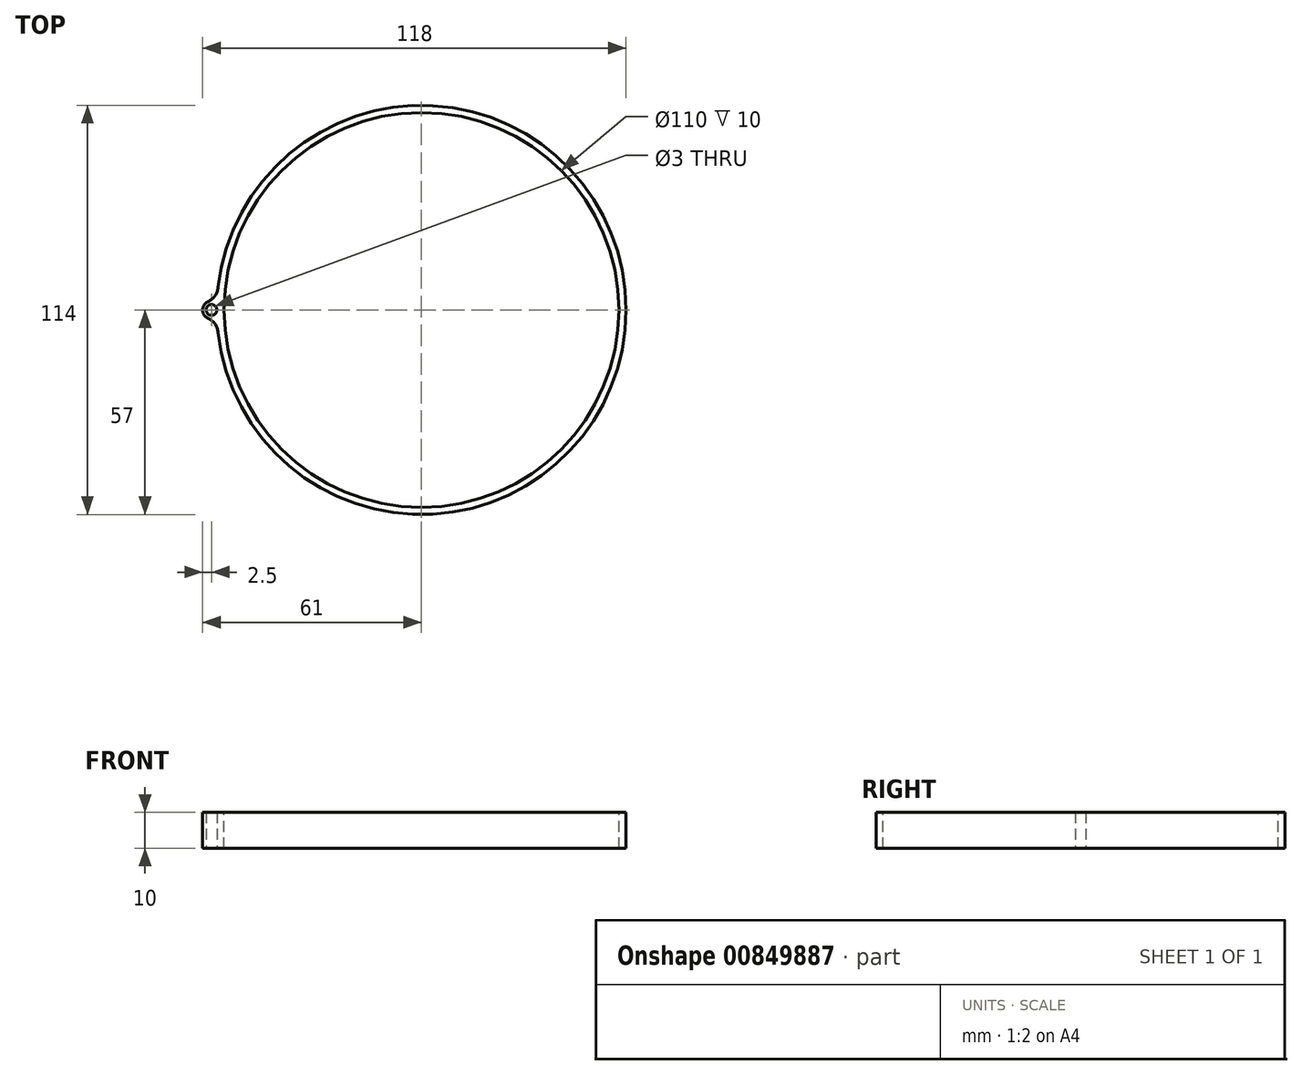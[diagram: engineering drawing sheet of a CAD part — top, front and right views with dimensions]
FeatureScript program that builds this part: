
annotation { "Feature Type Name" : "Feature", "Feature Type Description" : "" }
export const myFeature = defineFeature(function(context is Context, id is Id, definition is map)
    precondition{}
    {
        {
            var Q0;
            Q0=qCreatedBy(makeId("Top.planeOp"),FACE);
            var sketch = newSketch(context, id + "F0", { "sketchPlane" : qUnion([Q0])});
            skCircle(sketch, "E0", {"center": v(0, 0) * mm, "radius": 57 * mm});
            skSolve(sketch);
        }
        {
            var Q0;
            Q0=makeQuery(id+"F0.imprint","IMPRINT",FACE,{"disambiguationData":[TD([[makeQuery(id+"F0.imprint","IMPRINT",EDGE,{"derivedFrom":sQuery(id+"F0.wireOp",EDGE,"E0")}),1.0]])]});
            extrude(context, id + "F1", {"entities" : qUnion([Q0]), "depth" : 10 * mm, "offsetDistance" : 25 * mm});
        }
        {
            var Q0;
            Q0=makeQuery(id+"F1.opExtrude","CAP_FACE",FACE,{"disambiguationData":[OSD([sQuery(id+"F0.wireOp",EDGE,"E0")])],"isStart":false});
            var sketch = newSketch(context, id + "F2", { "sketchPlane" : qUnion([Q0])});
            skCircle(sketch, "E1", {"center": v(0, 0) * mm, "radius": 55 * mm});
            skSolve(sketch);
        }
        {
            var Q0;
            Q0=makeQuery(id+"F2.imprint","IMPRINT",FACE,{"disambiguationData":[TD([[makeQuery(id+"F2.imprint","IMPRINT",EDGE,{"derivedFrom":sQuery(id+"F2.wireOp",EDGE,"E1")}),1.0]])]});
            var Q1;
            Q1=sQuery(id+"F2.wireOp",EDGE,"E1");
            extrude(context, id + "F3", {"entities" : qUnion([Q0]), "operationType" : NewBodyOperationType.REMOVE, "surfaceEntities" : qUnion([Q1]), "oppositeDirection" : true, "depth" : 25 * mm, "offsetDistance" : 25 * mm});
        }
        {
            var Q0;
            Q0=qCreatedBy(makeId("Top.planeOp"),FACE);
            var sketch = newSketch(context, id + "F4", { "sketchPlane" : qUnion([Q0])});
            skCircle(sketch, "E2", {"center": v(-58.5, 0) * mm, "radius": 1.5 * mm});
            skCircle(sketch, "E3", {"center": v(-58.5, 0) * mm, "radius": 2.5 * mm});
            skSolve(sketch);
        }
        {
            var Q0;
            Q0 = qSketchRegion(id + "F4", true);
            extrude(context, id + "F5", {"entities" : qUnion([Q0]), "operationType" : NewBodyOperationType.ADD, "depth" : 10 * mm, "offsetDistance" : 25 * mm});
        }
        {
            var Q0;
            Q0=makeQuery(id+"F5.boolean.opBoolean","INTERSECT",EDGE,{"disambiguationData":[OD(1.0)],"derivedFrom":[makeQuery(id+"F1.opExtrude","SWEPT_FACE",FACE,{"disambiguationData":[OSD([sQuery(id+"F0.wireOp",EDGE,"E0")])]}),makeQuery(id+"F5.opExtrude","SWEPT_FACE",FACE,{"disambiguationData":[OSD([sQuery(id+"F4.wireOp",EDGE,"E3")])]})]});
            var Q1;
            Q1=makeQuery(id+"F5.boolean.opBoolean","INTERSECT",EDGE,{"disambiguationData":[OD(0.0)],"derivedFrom":[makeQuery(id+"F1.opExtrude","SWEPT_FACE",FACE,{"disambiguationData":[OSD([sQuery(id+"F0.wireOp",EDGE,"E0")])]}),makeQuery(id+"F5.opExtrude","SWEPT_FACE",FACE,{"disambiguationData":[OSD([sQuery(id+"F4.wireOp",EDGE,"E3")])]})]});
            fillet(context, id + "F6", {"entities" : qUnion([Q0, Q1]), "radius" : 5 * mm, "tangentPropagation" : true, "allowEdgeOverflow" : false});
        }
    });
